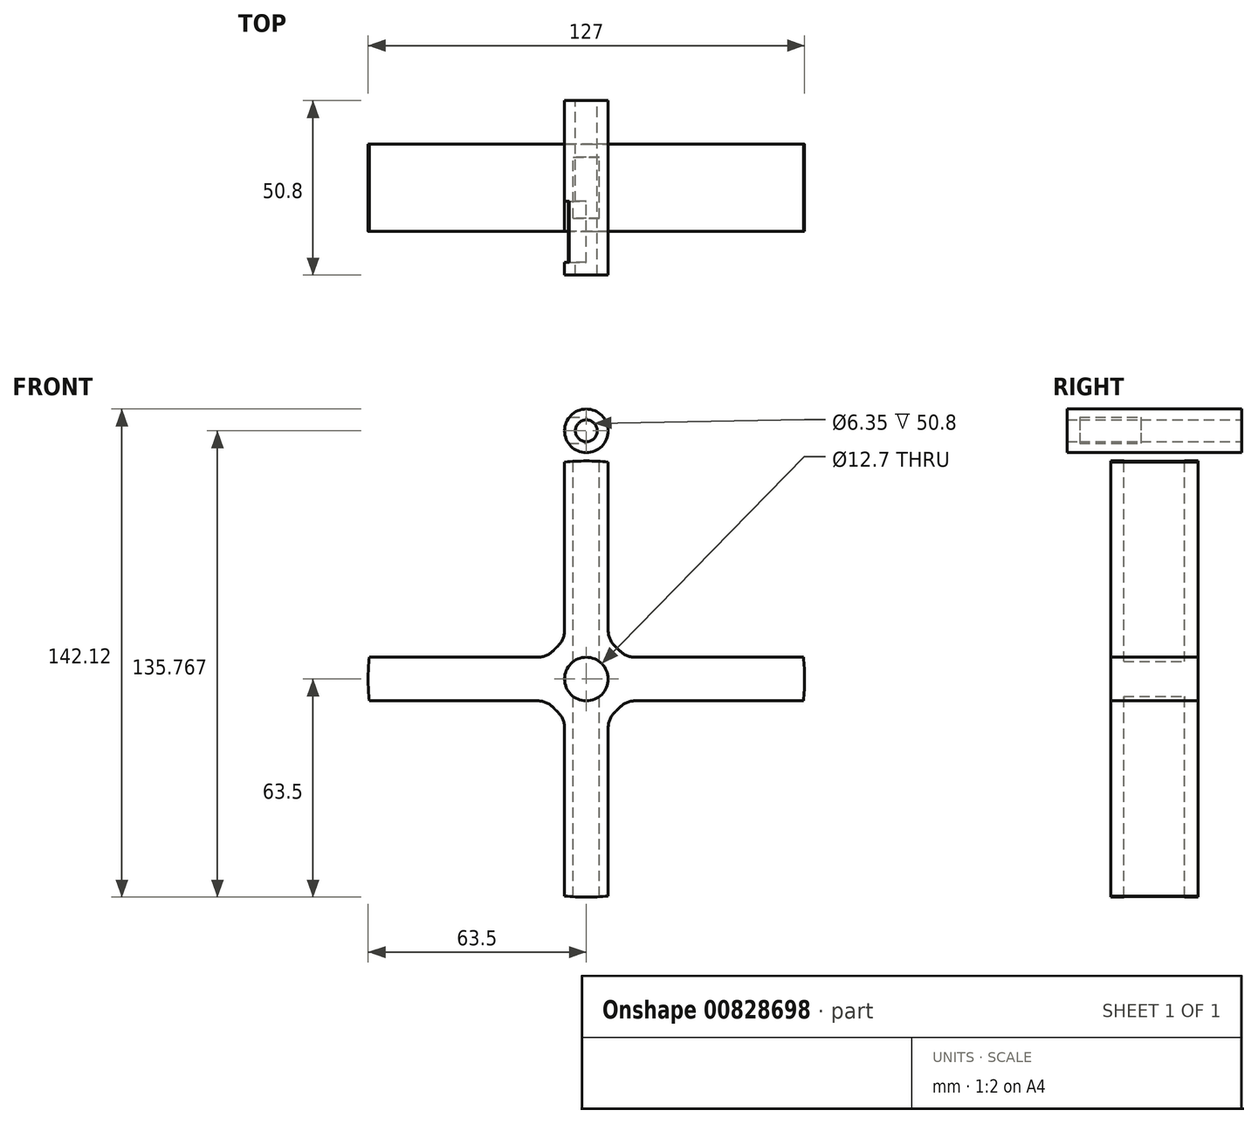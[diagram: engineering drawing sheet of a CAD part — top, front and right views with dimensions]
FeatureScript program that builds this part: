
annotation { "Feature Type Name" : "Feature", "Feature Type Description" : "" }
export const myFeature = defineFeature(function(context is Context, id is Id, definition is map)
    precondition{}
    {
        {
            var Q0;
            Q0=qCreatedBy(makeId("Front.planeOp"),FACE);
            var sketch = newSketch(context, id + "F0", { "sketchPlane" : qUnion([Q0])});
            skArc(sketch, "E0", {"start": v(6.35, 63.18) * mm, "mid": v(0, 63.5) * mm, "end": v(-6.35, 63.18) * mm});
            skArc(sketch, "E1", {"start": v(-8.47, 9.47) * mm, "mid": v(-8.98, 8.98) * mm, "end": v(-9.47, 8.47) * mm});
            skLineSegment(sketch, "E2", {"start": v(-6.35, 63.18) * mm, "end": v(-6.35, 14.2) * mm});
            skLineSegment(sketch, "E3", {"start": v(-63.18, 6.35) * mm, "end": v(-14.2, 6.35) * mm});
            skLineSegment(sketch, "E4", {"start": v(63.18, -6.35) * mm, "end": v(14.2, -6.35) * mm});
            skLineSegment(sketch, "E5", {"start": v(6.35, 63.18) * mm, "end": v(6.35, 14.2) * mm});
            skPoint(sketch, "E6.orphan", {"position": v(76.76, 6.35) * mm});
            skPoint(sketch, "E7.orphan", {"position": v(76.76, -6.35) * mm});
            skLineSegment(sketch, "E8.trimOffspring", {"start": v(-6.35, -14.2) * mm, "end": v(-6.35, -63.18) * mm});
            skLineSegment(sketch, "E9.trimOffspring", {"start": v(14.2, 6.35) * mm, "end": v(63.18, 6.35) * mm});
            skLineSegment(sketch, "E10.trimOffspring", {"start": v(-14.2, -6.35) * mm, "end": v(-63.18, -6.35) * mm});
            skLineSegment(sketch, "E11.trimOffspring", {"start": v(6.35, -14.2) * mm, "end": v(6.35, -63.18) * mm});
            skArc(sketch, "E12.trimOffspring", {"start": v(-63.18, 6.35) * mm, "mid": v(-63.5, 0) * mm, "end": v(-63.18, -6.35) * mm});
            skArc(sketch, "E13.trimOffspring", {"start": v(-6.35, -63.18) * mm, "mid": v(0, -63.5) * mm, "end": v(6.35, -63.18) * mm});
            skArc(sketch, "E14.trimOffspring", {"start": v(63.18, -6.35) * mm, "mid": v(63.5, 0) * mm, "end": v(63.18, 6.35) * mm});
            skCircle(sketch, "E15", {"center": v(0, 0) * mm, "radius": 6.35 * mm});
            skArc(sketch, "E16.trimOffspring", {"start": v(-9.47, -8.47) * mm, "mid": v(-8.98, -8.98) * mm, "end": v(-8.47, -9.47) * mm});
            skArc(sketch, "E17.trimOffspring", {"start": v(8.47, -9.47) * mm, "mid": v(8.98, -8.98) * mm, "end": v(9.47, -8.47) * mm});
            skArc(sketch, "E18.trimOffspring", {"start": v(9.47, 8.47) * mm, "mid": v(8.98, 8.98) * mm, "end": v(8.47, 9.47) * mm});
            skPoint(sketch, "E19.visualSharp", {"position": v(-6.35, 11) * mm});
            skArc(sketch, "E19.filletArc", {"start": v(-8.47, 9.47) * mm, "mid": v(-6.9, 11.6) * mm, "end": v(-6.35, 14.2) * mm});
            skPoint(sketch, "E20.visualSharp", {"position": v(-11, 6.35) * mm});
            skArc(sketch, "E20.filletArc", {"start": v(-14.2, 6.35) * mm, "mid": v(-11.6, 6.9) * mm, "end": v(-9.47, 8.47) * mm});
            skPoint(sketch, "E21.visualSharp", {"position": v(6.35, 11) * mm});
            skArc(sketch, "E21.filletArc", {"start": v(6.35, 14.2) * mm, "mid": v(6.9, 11.6) * mm, "end": v(8.47, 9.47) * mm});
            skPoint(sketch, "E22.visualSharp", {"position": v(11, 6.35) * mm});
            skArc(sketch, "E22.filletArc", {"start": v(9.47, 8.47) * mm, "mid": v(11.6, 6.9) * mm, "end": v(14.2, 6.35) * mm});
            skPoint(sketch, "E23.visualSharp", {"position": v(11, -6.35) * mm});
            skArc(sketch, "E23.filletArc", {"start": v(14.2, -6.35) * mm, "mid": v(11.6, -6.9) * mm, "end": v(9.47, -8.47) * mm});
            skPoint(sketch, "E24.visualSharp", {"position": v(6.35, -11) * mm});
            skArc(sketch, "E24.filletArc", {"start": v(8.47, -9.47) * mm, "mid": v(6.9, -11.6) * mm, "end": v(6.35, -14.2) * mm});
            skPoint(sketch, "E25.visualSharp", {"position": v(-6.35, -11) * mm});
            skArc(sketch, "E25.filletArc", {"start": v(-6.35, -14.2) * mm, "mid": v(-6.9, -11.6) * mm, "end": v(-8.47, -9.47) * mm});
            skPoint(sketch, "E26.visualSharp", {"position": v(-11, -6.35) * mm});
            skArc(sketch, "E26.filletArc", {"start": v(-9.47, -8.47) * mm, "mid": v(-11.6, -6.9) * mm, "end": v(-14.2, -6.35) * mm});
            skSolve(sketch);
        }
        {
            var Q0;
            Q0=qSketchRegion(id+"F0",true);
            extrude(context, id + "F1", {"entities" : qUnion([Q0]), "depth" : 25.4 * mm, "offsetDistance" : 25.4 * mm, "symmetric" : true});
        }
        {
            var Q0;
            Q0=qCreatedBy(makeId("Top.planeOp"),FACE);
            var sketch = newSketch(context, id + "F2", { "sketchPlane" : qUnion([Q0])});
            skLineSegment(sketch, "E27", {"start": v(-3.81, 8.9) * mm, "end": v(-3.8, -8.9) * mm});
            skLineSegment(sketch, "E28", {"start": v(3.8, 8.9) * mm, "end": v(3.81, -8.9) * mm});
            skLineSegment(sketch, "E29", {"start": v(3.81, -8.9) * mm, "end": v(-3.8, -8.9) * mm});
            skLineSegment(sketch, "E30", {"start": v(3.8, 8.9) * mm, "end": v(-3.81, 8.9) * mm});
            skPoint(sketch, "E31.orphan", {"position": v(3.81, -31.13) * mm});
            skPoint(sketch, "E32.orphan", {"position": v(-3.8, -31.13) * mm});
            skSolve(sketch);
        }
        {
            var Q0;
            Q0=qSketchRegion(id+"F2",true);
            extrude(context, id + "F3", {"entities" : qUnion([Q0]), "operationType" : NewBodyOperationType.REMOVE, "oppositeDirection" : true, "depth" : 127 * mm, "offsetDistance" : 25.4 * mm, "symmetric" : true});
        }
        {
            var Q0;
            Q0=qCreatedBy(makeId("Front.planeOp"),FACE);
            var sketch = newSketch(context, id + "F4", { "sketchPlane" : qUnion([Q0])});
            skCircle(sketch, "E33", {"center": v(0, 72.27) * mm, "radius": 6.35 * mm});
            skCircle(sketch, "E34", {"center": v(0, -71.12) * mm, "radius": 6.35 * mm});
            skCircle(sketch, "E35", {"center": v(0, 72.27) * mm, "radius": 3.18 * mm});
            skSolve(sketch);
        }
        {
            var Q0;
            Q0=makeQuery(id+"F4.imprint","IMPRINT",FACE,{"disambiguationData":[TD([[makeQuery(id+"F4.imprint","IMPRINT",EDGE,{"derivedFrom":sQuery(id+"F4.wireOp",EDGE,"E33")}),1.0]])]});
            extrude(context, id + "F5", {"entities" : qUnion([Q0]), "depth" : 50.8 * mm, "offsetDistance" : 25.4 * mm, "symmetric" : true});
        }
        {
            var Q0;
            Q0=qCreatedBy(makeId("Right.planeOp"),FACE);
            var sketch = newSketch(context, id + "F6", { "sketchPlane" : qUnion([Q0])});
            skLineSegment(sketch, "E36.bottom", {"start": v(-3.93, 76.25) * mm, "end": v(-21.71, 76.25) * mm});
            skLineSegment(sketch, "E36.top", {"start": v(-3.93, 68.63) * mm, "end": v(-21.71, 68.63) * mm});
            skLineSegment(sketch, "E36.left", {"start": v(-3.93, 76.25) * mm, "end": v(-3.93, 68.63) * mm});
            skLineSegment(sketch, "E36.right", {"start": v(-21.71, 76.25) * mm, "end": v(-21.71, 68.63) * mm});
            skSolve(sketch);
        }
        {
            var Q0;
            Q0=makeQuery(id+"F6.imprint","IMPRINT",FACE,{"disambiguationData":[TD([[makeQuery(id+"F6.imprint","IMPRINT",EDGE,{"derivedFrom":sQuery(id+"F6.wireOp",EDGE,"E36.bottom")}),1.0]])]});
            extrude(context, id + "F7", {"entities" : qUnion([Q0]), "operationType" : NewBodyOperationType.REMOVE, "oppositeDirection" : true, "depth" : 7.62 * mm, "offsetDistance" : 25.4 * mm});
        }
    });
